# Revit family: Sink-Vessel-Lavatory-KOHLER-Shagreen_Round-K-77714_1
name_source: partatom
category: Plumbing Fixtures
revit_build: Autodesk Revit 2017 (Build: 20160225_1515(x64)
units: mm (PartAtom-declared; Revit-internal decimal feet)

## family parameters
Cut with Voids When Loaded = No
Host = Face
OmniClass Number = 23.31.13.00
OmniClass Title = Sinks
Part Type = Normal
Room Calculation Point = No
Round Connector Dimension = Use Diameter
Shared = No

## types (2) — shared parameters
ADA Compliant = Yes
Assembly Code = D2010400
CW Connection = No
Cold Water Inlet = Cold Water Inlet
Date Modified = 02/09/2021
Default Elevation = 36"
Description = Round Wading Pool
Drain Included = No
HW Connection = No
Height = 6"
Hot Water Inlet = Hot Water Inlet
Length = 17 11/16"
Manufacturer = KOHLER Co.
Master Format 2014 = 22 41 16
Master Format 2014 Name = Residential Lavatories and Sinks
Material = Vitreous china
Product Documentation Link = https://www.us.kohler.com
Product Name = Shagreen_Rectangle
Product Page URL = http://www.us.kohler.com
URL = https://www.us.kohler.com
Vent Connection = No
Waste Connection = Yes
Waste Water Outlet = Waste Water Outlet
WaterSense Certified = No
Width = 17 11/16"

## per-type parameters (varying)
| type | Finish | Model | Type |
| SSP-Oyster_Pearl | KOHLER-Vitreous_China-SSP-Oyster_Pearl | K-77714-SSP | 1 |
| TB2-Ebony_Pearl | KOHLER-Vitreous_China-TB2-Ebony_Pearl | K-77714-TB2 | 2 |

## geometry (parser evidence)
native form markers: Sweep x4
no freeform markers — native parametric forms only
